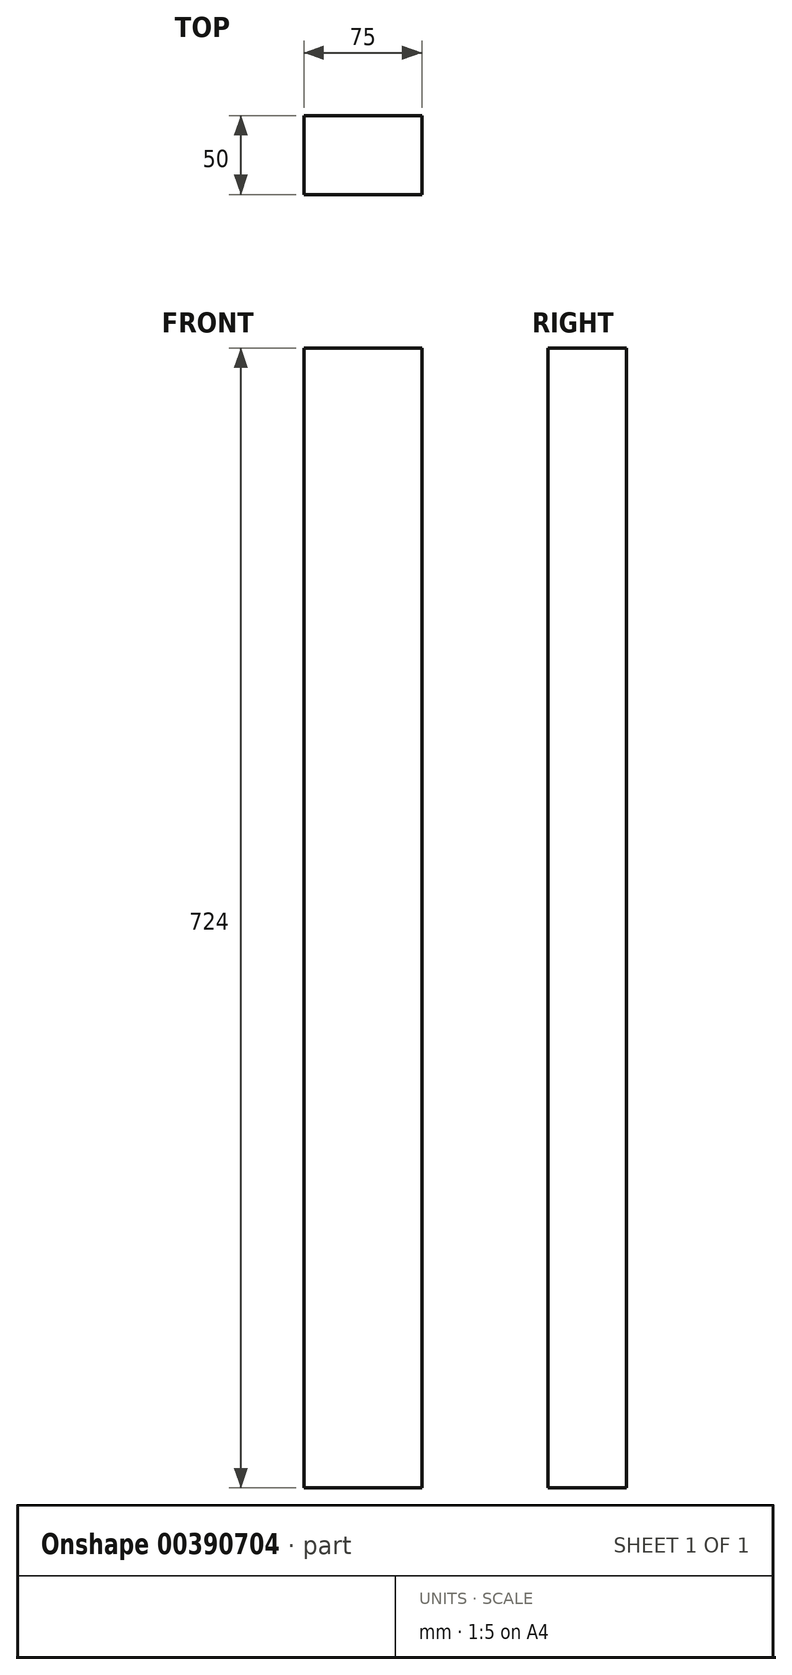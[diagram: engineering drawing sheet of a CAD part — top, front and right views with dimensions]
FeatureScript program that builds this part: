
annotation { "Feature Type Name" : "Feature", "Feature Type Description" : "" }
export const myFeature = defineFeature(function(context is Context, id is Id, definition is map)
    precondition{}
    {
        {
            var Q0;
            Q0=qCreatedBy(makeId("Top.planeOp"),FACE);
            var sketch = newSketch(context, id + "F0", { "sketchPlane" : qUnion([Q0])});
            skLineSegment(sketch, "E0.bottom", {"start": v(0, 0) * mm, "end": v(75, 0) * mm});
            skLineSegment(sketch, "E0.top", {"start": v(0, 50) * mm, "end": v(75, 50) * mm});
            skLineSegment(sketch, "E0.left", {"start": v(0, 0) * mm, "end": v(0, 50) * mm});
            skLineSegment(sketch, "E0.right", {"start": v(75, 0) * mm, "end": v(75, 50) * mm});
            skSolve(sketch);
        }
        {
            var Q0;
            Q0=qSketchRegion(id+"F0",true);
            extrude(context, id + "F1", {"entities" : qUnion([Q0]), "depth" : 724 * mm});
        }
    });
